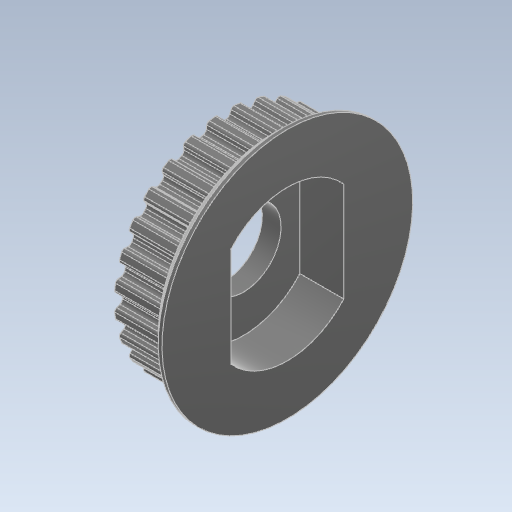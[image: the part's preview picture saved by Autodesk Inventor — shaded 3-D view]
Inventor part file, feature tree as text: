
AUTODESK INVENTOR PART (.ipt)
format: ipt  version: 2024 (Build 280153000, 153)  size: 555,008 bytes
history: native  units: mm
features: other x5, sketch x2, revolve x1, extrude x1
ambient origin geometry x8: Origin, YZ Plane, XZ Plane, XY Plane, X Axis, Y Axis, Z Axis, Center Point
bodies: Solid1 (feature_tree)
feature tree (9):
  other  "brideye_elbowUnit_pully-origin.ipt"
  revolve  "回転6"
  extrude  "押し出し2"  Depth=10.0mm
  other  "厚み2"
  sketch  "スケッチ3"
  other  "Solid1::brideye_elbowUnit_pully-origin.ipt"
  other  "TaggingFeature2"
  other  "スケッチ3_1"
  sketch  "スケッチ5"
